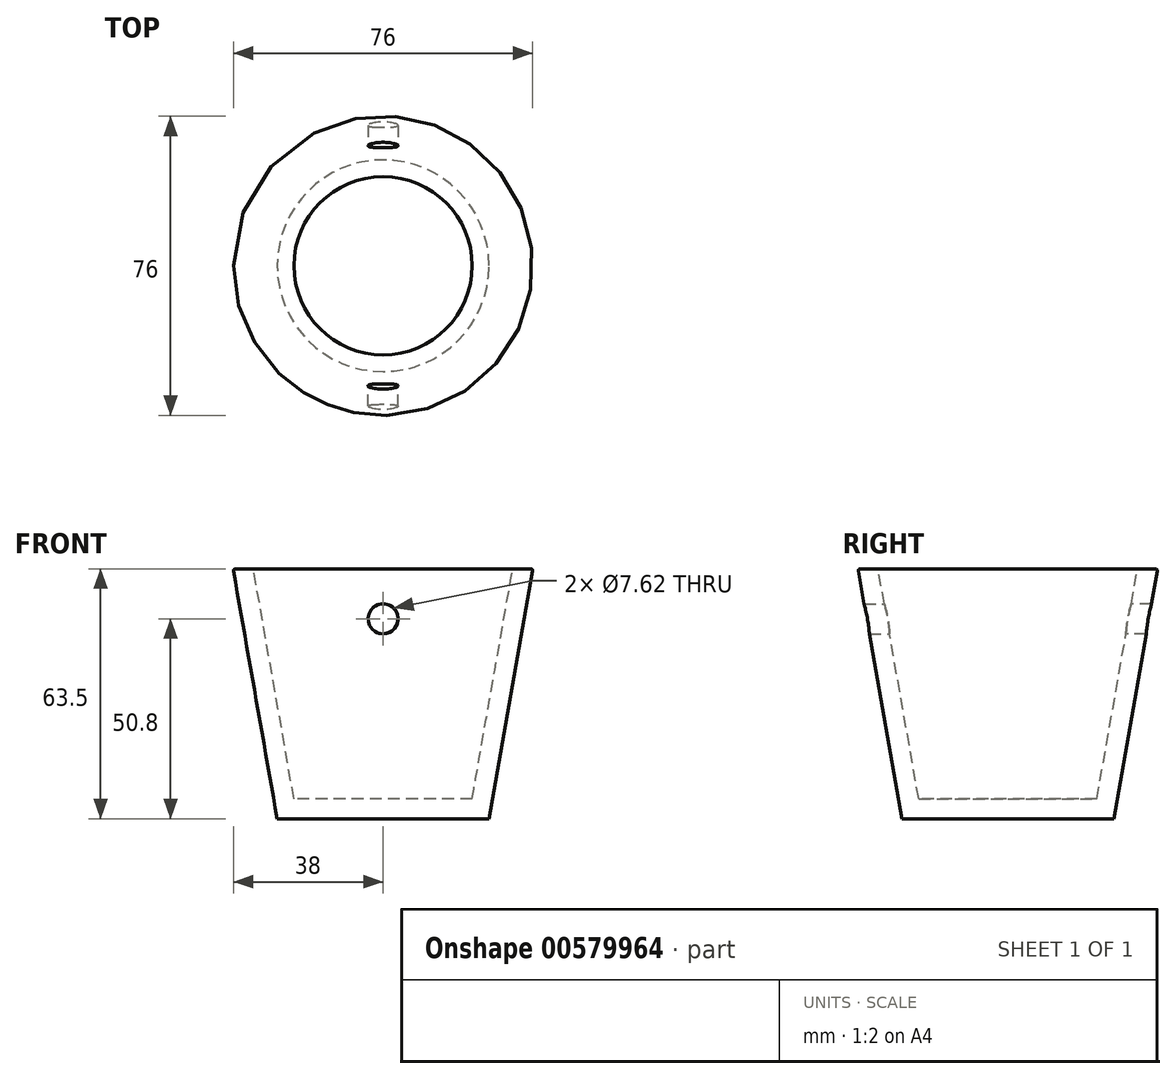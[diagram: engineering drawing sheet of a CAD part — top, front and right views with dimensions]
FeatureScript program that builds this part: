
annotation { "Feature Type Name" : "Feature", "Feature Type Description" : "" }
export const myFeature = defineFeature(function(context is Context, id is Id, definition is map)
    precondition{}
    {
        {
            var Q0;
            Q0=qCreatedBy(makeId("Front.planeOp"),FACE);
            var sketch = newSketch(context, id + "F0", { "sketchPlane" : qUnion([Q0])});
            skLineSegment(sketch, "E0", {"start": v(0, 63.5) * mm, "end": v(-38.1, 63.5) * mm});
            skLineSegment(sketch, "E1", {"start": v(-38.1, 63.5) * mm, "end": v(-26.9, 0) * mm});
            skLineSegment(sketch, "E2", {"start": v(-26.9, 0) * mm, "end": v(0, 0) * mm});
            skLineSegment(sketch, "E3", {"start": v(0, 0) * mm, "end": v(0, 63.5) * mm});
            skSolve(sketch);
        }
        {
            var Q0;
            Q0=makeQuery(id+"F0.imprint","IMPRINT",FACE,{"disambiguationData":[TD([[makeQuery(id+"F0.imprint","IMPRINT",EDGE,{"derivedFrom":sQuery(id+"F0.wireOp",EDGE,"E0")}),1.0]])]});
            var Q1;
            Q1=sQuery(id+"F0.wireOp",EDGE,"E3");
            revolve(context, id + "F1", {"entities" : qUnion([Q0]), "axis" : qUnion([Q1]), "revolveType" : RevolveType.FULL});
        }
        {
            var Q0;
            Q0=makeQuery(id+"F1.opRevolve","SWEPT_FACE",FACE,{"disambiguationData":[OSD([sQuery(id+"F0.wireOp",EDGE,"E0")])]});
            shell(context, id + "F2", {"entities" : qUnion([Q0]), "thickness" : 5.08 * mm});
        }
        {
            var Q0;
            Q0=qCreatedBy(makeId("Front.planeOp"),FACE);
            var sketch = newSketch(context, id + "F3", { "sketchPlane" : qUnion([Q0])});
            skLineSegment(sketch, "E4", {"start": v(38.1, 63.5) * mm, "end": v(26.9, 0) * mm});
            skLineSegment(sketch, "E5", {"start": v(-26.9, 0) * mm, "end": v(-38.1, 63.5) * mm});
            skLineSegment(sketch, "E6.0", {"start": v(38.1, 63.5) * mm, "end": v(-38.1, 63.5) * mm});
            skLineSegment(sketch, "E7", {"start": v(0, 63.5) * mm, "end": v(0, 50.8) * mm});
            skPoint(sketch, "E7.endSnap0", {"position": v(0, 63.5) * mm});
            skCircle(sketch, "E8", {"center": v(0, 50.8) * mm, "radius": 3.81 * mm});
            skSolve(sketch);
        }
        {
            var Q0;
            Q0=makeQuery(id+"F3.imprint","IMPRINT",FACE,{"disambiguationData":[TD([[makeQuery(id+"F3.imprint","IMPRINT",EDGE,{"derivedFrom":sQuery(id+"F3.wireOp",EDGE,"E8")}),1.0]])]});
            extrude(context, id + "F4", {"entities" : qUnion([Q0]), "operationType" : NewBodyOperationType.REMOVE, "endBound" : BoundingType.THROUGH_ALL, "depth" : 25.4 * mm, "offsetDistance" : 25.4 * mm});
        }
        {
            var Q0;
            Q0 = qSketchRegion(id + "F3", true);
            extrude(context, id + "F5", {"entities" : qUnion([Q0]), "operationType" : NewBodyOperationType.REMOVE, "endBound" : BoundingType.THROUGH_ALL, "oppositeDirection" : true, "depth" : 25.4 * mm, "offsetDistance" : 25.4 * mm});
        }
        {
            var Q0;
            Q0=makeQuery(id+"F1.opRevolve","SWEPT_EDGE",EDGE,{"disambiguationData":[OSD([sQuery(id+"F0.wireOp",EDGE,"E0"),sQuery(id+"F0.wireOp",EDGE,"E1")])]});
            var Q1;
            Q1=makeQuery(id+"F2.opShell","OFFSET_EDGE",EDGE,{"disambiguationData":[OSD([sQuery(id+"F0.wireOp",EDGE,"E0"),sQuery(id+"F0.wireOp",EDGE,"E1")])]});
            fillet(context, id + "F6", {"entities" : qUnion([Q0, Q1]), "radius" : 0.5 * mm, "tangentPropagation" : true, "allowEdgeOverflow" : false});
        }
    });
